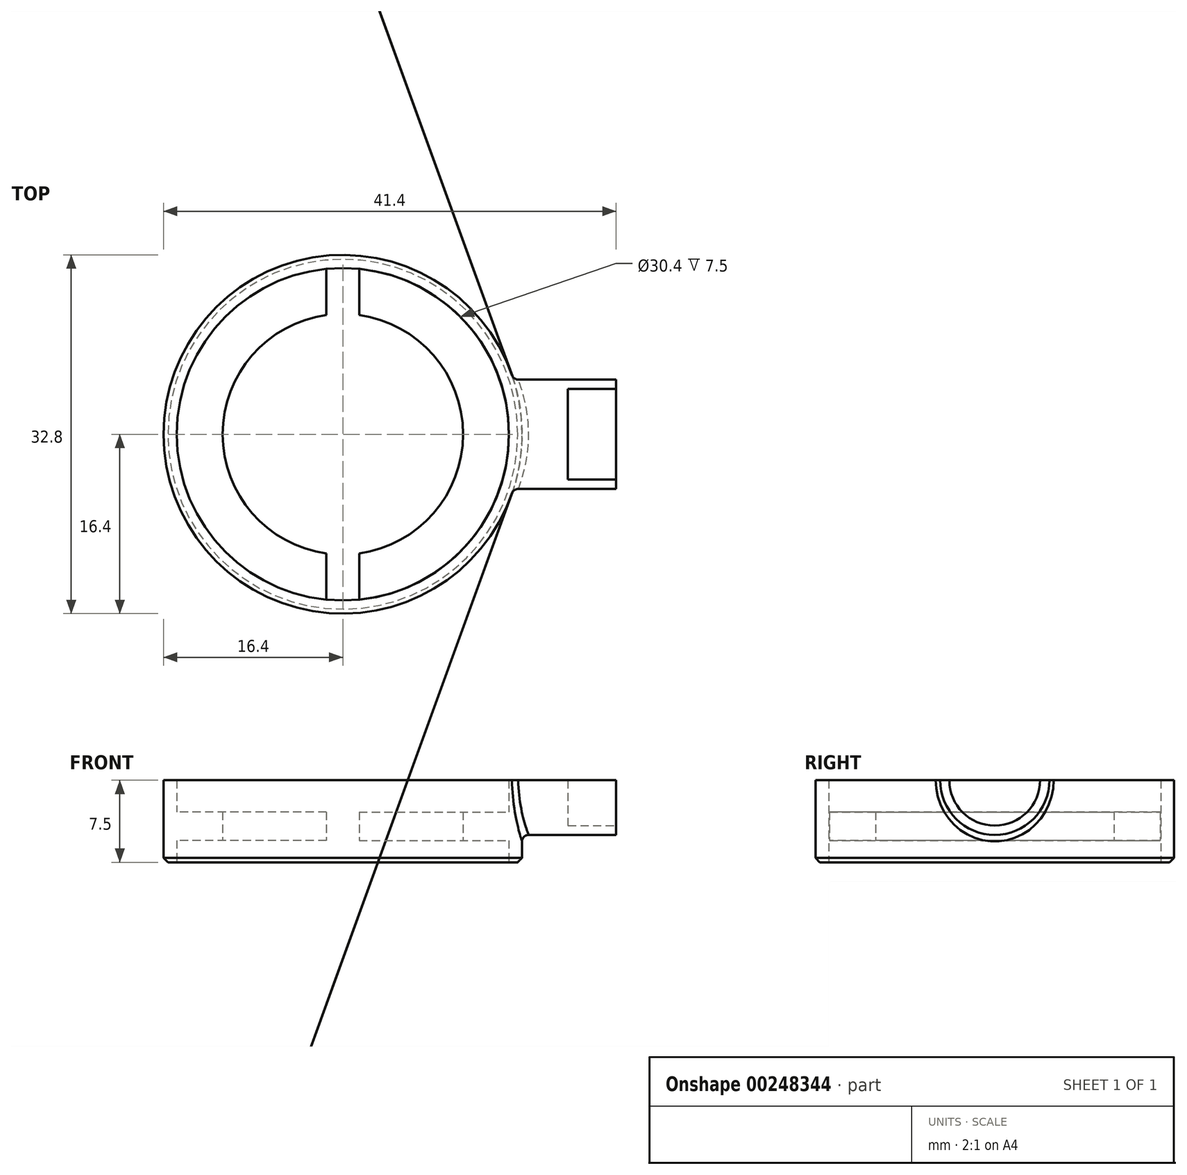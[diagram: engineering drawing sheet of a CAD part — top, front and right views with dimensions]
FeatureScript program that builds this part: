
annotation { "Feature Type Name" : "Feature", "Feature Type Description" : "" }
export const myFeature = defineFeature(function(context is Context, id is Id, definition is map)
    precondition{}
    {
        {
            var Q0;
            Q0=qCreatedBy(makeId("Top.planeOp"),FACE);
            var sketch = newSketch(context, id + "F0", { "sketchPlane" : qUnion([Q0])});
            skCircle(sketch, "E0", {"center": v(0, 0) * mm, "radius": 16.4 * mm});
            skSolve(sketch);
        }
        {
            var Q0;
            Q0=qSketchRegion(id+"F0",true);
            extrude(context, id + "F1", {"entities" : qUnion([Q0]), "depth" : 15 * mm});
        }
        {
            var Q0;
            Q0=makeQuery(id+"F1.opExtrude","CAP_FACE",FACE,{"disambiguationData":[OSD([sQuery(id+"F0.wireOp",EDGE,"E0")])],"isStart":true});
            var sketch = newSketch(context, id + "F2", { "sketchPlane" : qUnion([Q0])});
            skCircle(sketch, "E1", {"center": v(0, 0) * mm, "radius": 15.2 * mm});
            skSolve(sketch);
        }
        {
            var Q0;
            Q0=qSketchRegion(id+"F2",true);
            extrude(context, id + "F3", {"entities" : qUnion([Q0]), "operationType" : NewBodyOperationType.REMOVE, "oppositeDirection" : true, "depth" : 2 * mm});
        }
        {
            var Q0;
            Q0=makeQuery(id+"F3.boolean.opBoolean","COPY",FACE,{"derivedFrom":makeQuery(id+"F3.opExtrude","CAP_FACE",FACE,{"disambiguationData":[OSD([sQuery(id+"F2.wireOp",EDGE,"E1")])],"isStart":false})});
            var sketch = newSketch(context, id + "F4", { "sketchPlane" : qUnion([Q0])});
            skCircle(sketch, "E2", {"center": v(0, 0) * mm, "radius": 11 * mm});
            skSolve(sketch);
        }
        {
            var Q0;
            Q0=qSketchRegion(id+"F4",true);
            extrude(context, id + "F5", {"entities" : qUnion([Q0]), "operationType" : NewBodyOperationType.REMOVE, "oppositeDirection" : true, "depth" : 25 * mm});
        }
        {
            var Q0;
            Q0=makeQuery(id+"F1.opExtrude","CAP_FACE",FACE,{"disambiguationData":[OSD([sQuery(id+"F0.wireOp",EDGE,"E0")])],"isStart":false});
            var sketch = newSketch(context, id + "F6", { "sketchPlane" : qUnion([Q0])});
            skCircle(sketch, "E3", {"center": v(0, 0) * mm, "radius": 15.2 * mm});
            skSolve(sketch);
        }
        {
            var Q0;
            Q0=qSketchRegion(id+"F6",true);
            extrude(context, id + "F7", {"entities" : qUnion([Q0]), "operationType" : NewBodyOperationType.REMOVE, "oppositeDirection" : true, "depth" : 10.4 * mm});
        }
        {
            var Q0;
            Q0=makeQuery(id+"F1.opExtrude","CAP_FACE",FACE,{"disambiguationData":[OSD([sQuery(id+"F0.wireOp",EDGE,"E0")])],"isStart":false});
            var sketch = newSketch(context, id + "F8", { "sketchPlane" : qUnion([Q0])});
            skCircle(sketch, "E4", {"center": v(0, 0) * mm, "radius": 15.5 * mm});
            skSolve(sketch);
        }
        {
            var Q0;
            Q0=qSketchRegion(id+"F8",true);
            extrude(context, id + "F9", {"entities" : qUnion([Q0]), "operationType" : NewBodyOperationType.ADD, "oppositeDirection" : true, "depth" : 6 * mm});
        }
        {
            var Q0;
            Q0=makeQuery(id+"F9.opExtrude","CAP_FACE",FACE,{"disambiguationData":[OSD([sQuery(id+"F8.wireOp",EDGE,"E4")])],"isStart":false});
            var sketch = newSketch(context, id + "F10", { "sketchPlane" : qUnion([Q0])});
            skCircle(sketch, "E5", {"center": v(0, 0) * mm, "radius": 6.2 * mm});
            skSolve(sketch);
        }
        {
            var Q0;
            Q0=qSketchRegion(id+"F10",true);
            extrude(context, id + "F11", {"entities" : qUnion([Q0]), "operationType" : NewBodyOperationType.REMOVE, "oppositeDirection" : true, "depth" : 5 * mm});
        }
        {
            var Q0;
            Q0=makeQuery(id+"F3.boolean.opBoolean","COPY",FACE,{"derivedFrom":makeQuery(id+"F3.opExtrude","CAP_FACE",FACE,{"disambiguationData":[OSD([sQuery(id+"F2.wireOp",EDGE,"E1")])],"isStart":false})});
            var sketch = newSketch(context, id + "F12", { "sketchPlane" : qUnion([Q0])});
            skLineSegment(sketch, "E6.bottom", {"start": v(1.5, 18) * mm, "end": v(-1.5, 18) * mm});
            skLineSegment(sketch, "E6.top", {"start": v(1.5, -18) * mm, "end": v(-1.5, -18) * mm});
            skLineSegment(sketch, "E6.left", {"start": v(1.5, 18) * mm, "end": v(1.5, -18) * mm});
            skLineSegment(sketch, "E6.right", {"start": v(-1.5, 18) * mm, "end": v(-1.5, -18) * mm});
            skPoint(sketch, "E6.middle", {"position": v(0, 0) * mm});
            skCircle(sketch, "E7.0", {"center": v(0, 0) * mm, "radius": 15.2 * mm});
            skSolve(sketch);
        }
        {
            var Q0;
            {var subQ0=sQuery(id+"F12.wireOp",EDGE,"E7.0");var subQ1=sQuery(id+"F12.wireOp",EDGE,"E6.left");var subQ2=makeQuery(id+"F12.imprint","INTERSECT",VERTEX,{"disambiguationData":[OD(0.0)],"derivedFrom":[subQ1,subQ0]});Q0=makeQuery(id+"F12.imprint","IMPRINT",FACE,{"disambiguationData":[TD([[makeQuery(id+"F12.imprint","IMPRINT",EDGE,{"disambiguationData":[TD([[subQ2,-1.0]])],"derivedFrom":subQ1}),-1.0]])]});}
            var Q1;
            {var subQ0=sQuery(id+"F12.wireOp",EDGE,"E7.0");var subQ1=sQuery(id+"F12.wireOp",EDGE,"E6.left");var subQ2=makeQuery(id+"F12.imprint","INTERSECT",VERTEX,{"disambiguationData":[OD(1.0)],"derivedFrom":[subQ1,subQ0]});Q1=makeQuery(id+"F12.imprint","IMPRINT",FACE,{"disambiguationData":[TD([[makeQuery(id+"F12.imprint","IMPRINT",EDGE,{"disambiguationData":[TD([[subQ2,1.0]])],"derivedFrom":subQ1}),-1.0]])]});}
            extrude(context, id + "F13", {"entities" : qUnion([Q0, Q1]), "operationType" : NewBodyOperationType.REMOVE, "oppositeDirection" : true, "depth" : 5 * mm});
        }
        {
            var Q0;
            Q0=qCreatedBy(makeId("Right.planeOp"),FACE);
            var sketch = newSketch(context, id + "F14", { "sketchPlane" : qUnion([Q0])});
            skCircle(sketch, "E8", {"center": v(0, 7.5) * mm, "radius": 5 * mm});
            skSolve(sketch);
        }
        {
            var Q0;
            Q0=qSketchRegion(id+"F14",true);
            var Q1;
            Q1=makeQuery(id+"F1.opExtrude","SWEPT_BODY",BODY,{"disambiguationData":[OSD([sQuery(id+"F0.wireOp",EDGE,"E0")])]});
            extrude(context, id + "F15", {"entities" : qUnion([Q0]), "operationType" : NewBodyOperationType.ADD, "depth" : 25 * mm, "hasSecondDirection" : true, "secondDirectionBound" : SecondDirectionBoundingType.UP_TO_BODY, "secondDirectionOppositeDirection" : false, "secondDirectionBoundEntityBody" : qUnion([Q1]), "secondDirectionDepth" : 25 * mm});
        }
        {
            var Q0;
            Q0=makeQuery(id+"F15.boolean.opBoolean","INTERSECT",EDGE,{"derivedFrom":[makeQuery(id+"F1.opExtrude","SWEPT_FACE",FACE,{"disambiguationData":[OSD([sQuery(id+"F0.wireOp",EDGE,"E0")])]}),makeQuery(id+"F15.opExtrude","SWEPT_FACE",FACE,{"disambiguationData":[OSD([sQuery(id+"F14.wireOp",EDGE,"E8")])]})]});
            fillet(context, id + "F16", {"entities" : qUnion([Q0]), "radius" : 0.6 * mm, "tangentPropagation" : true, "allowEdgeOverflow" : false});
        }
        {
            var Q0;
            Q0=makeQuery(id+"F1.opExtrude","CAP_EDGE",EDGE,{"disambiguationData":[OSD([sQuery(id+"F0.wireOp",EDGE,"E0")])],"isStart":true});
            var Q1;
            Q1=makeQuery(id+"F1.opExtrude","CAP_EDGE",EDGE,{"disambiguationData":[OSD([sQuery(id+"F0.wireOp",EDGE,"E0")])],"isStart":false});
            chamfer(context, id + "F17", {"entities" : qUnion([Q0, Q1]), "width" : 0.4 * mm, "tangentPropagation" : true});
        }
        {
            var Q0;
            Q0=makeQuery(id+"F15.opExtrude","CAP_FACE",FACE,{"disambiguationData":[OSD([sQuery(id+"F14.wireOp",EDGE,"E8")])],"isStart":false});
            var sketch = newSketch(context, id + "F18", { "sketchPlane" : qUnion([Q0])});
            skCircle(sketch, "E9", {"center": v(0, 7.5) * mm, "radius": 4.15 * mm});
            skSolve(sketch);
        }
        {
            var Q0;
            Q0=qSketchRegion(id+"F18",true);
            extrude(context, id + "F19", {"entities" : qUnion([Q0]), "operationType" : NewBodyOperationType.REMOVE, "oppositeDirection" : true, "depth" : 4.4 * mm});
        }
        {
            var Q0;
            Q0=qCreatedBy(makeId("Top.planeOp"),FACE);
            cPlane(context, id + "F20", {"entities" : qUnion([Q0]), "cplaneType" : CPlaneType.OFFSET, "offset" : 7.5 * mm, "width" : 150 * mm, "height" : 150 * mm});
        }
        {
            var Q0;
            Q0=qCreatedBy(id+"F20.planeOp",FACE);
            var sketch = newSketch(context, id + "F21", { "sketchPlane" : qUnion([Q0])});
            skCircle(sketch, "E10", {"center": v(0, 0) * mm, "radius": 45.33 * mm});
            skSolve(sketch);
        }
        {
            var Q0;
            Q0=qSketchRegion(id+"F21",true);
            extrude(context, id + "F22", {"entities" : qUnion([Q0]), "operationType" : NewBodyOperationType.REMOVE, "depth" : 25 * mm});
        }
    });
